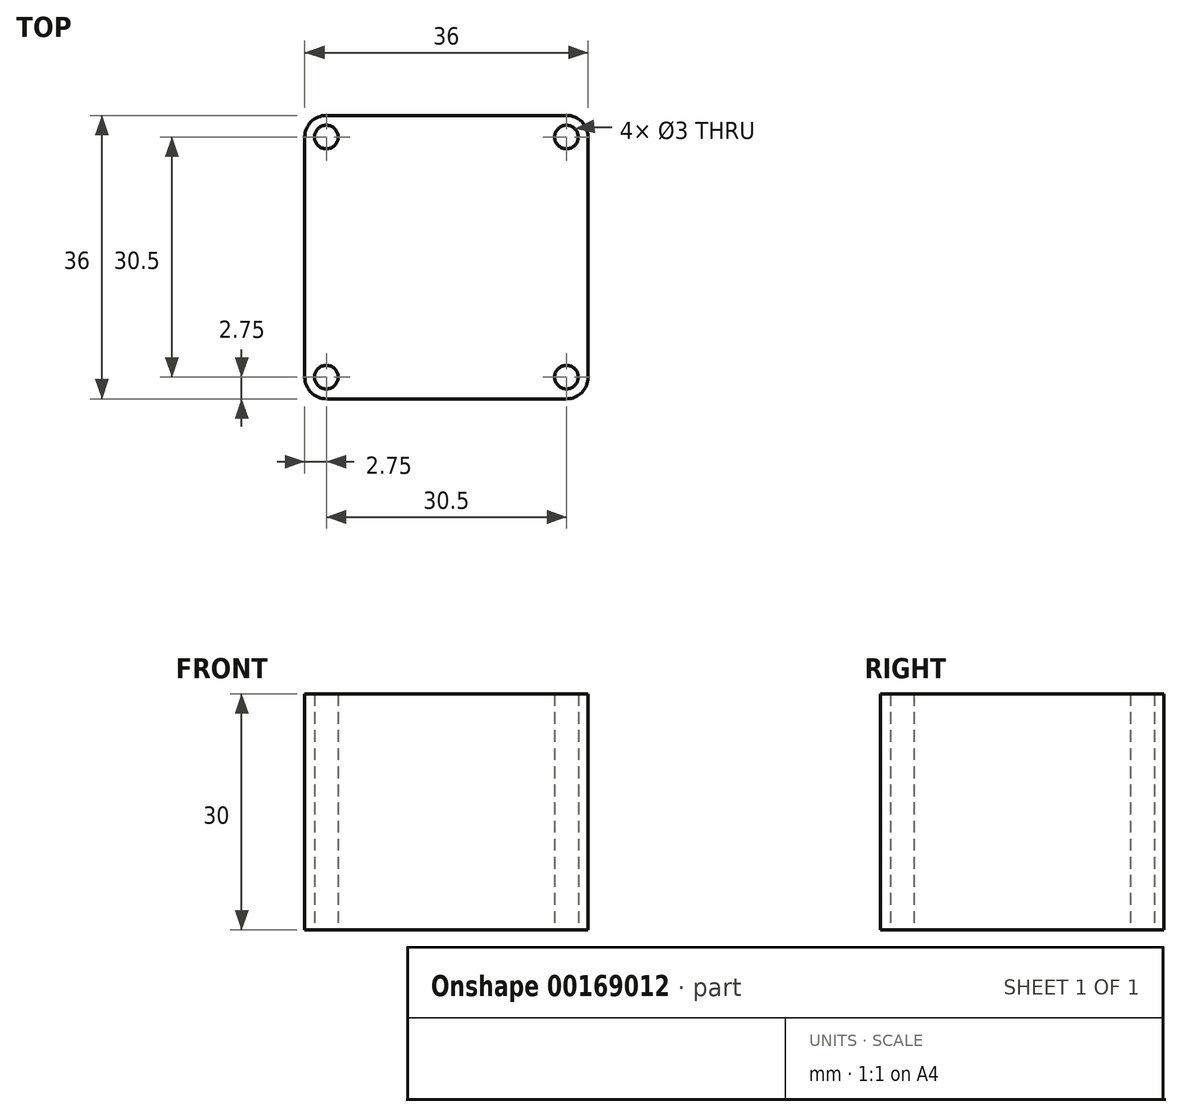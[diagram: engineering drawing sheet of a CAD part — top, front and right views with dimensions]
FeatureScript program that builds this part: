
annotation { "Feature Type Name" : "Feature", "Feature Type Description" : "" }
export const myFeature = defineFeature(function(context is Context, id is Id, definition is map)
    precondition{}
    {
        {
            var Q0;
            Q0=qCreatedBy(makeId("Top.planeOp"),FACE);
            var sketch = newSketch(context, id + "F0", { "sketchPlane" : qUnion([Q0])});
            skLineSegment(sketch, "E0.bottom", {"start": v(2.75, 36) * mm, "end": v(33.25, 36) * mm});
            skLineSegment(sketch, "E0.top", {"start": v(2.75, 0) * mm, "end": v(33.25, 0) * mm});
            skLineSegment(sketch, "E0.left", {"start": v(0, 33.25) * mm, "end": v(0, 2.75) * mm});
            skLineSegment(sketch, "E0.right", {"start": v(36, 33.25) * mm, "end": v(36, 2.75) * mm});
            skCircle(sketch, "E1", {"center": v(2.75, 2.75) * mm, "radius": 1.5 * mm});
            skCircle(sketch, "E2.0.1.0", {"center": v(2.75, 33.25) * mm, "radius": 1.5 * mm});
            skCircle(sketch, "E2.1.0.0", {"center": v(33.25, 2.75) * mm, "radius": 1.5 * mm});
            skCircle(sketch, "E2.1.1.0", {"center": v(33.25, 33.25) * mm, "radius": 1.5 * mm});
            skLineSegment(sketch, "E2.direction1", {"start": v(2.75, 2.75) * mm, "end": v(33.25, 2.75) * mm, "construction": true});
            skLineSegment(sketch, "E2.direction2", {"start": v(2.75, 2.75) * mm, "end": v(2.75, 33.25) * mm, "construction": true});
            skPoint(sketch, "E3.visualSharp", {"position": v(0, 36) * mm});
            skArc(sketch, "E3.filletArc", {"start": v(2.75, 36) * mm, "mid": v(0.8, 35.2) * mm, "end": v(0, 33.25) * mm});
            skPoint(sketch, "E4.visualSharp", {"position": v(36, 36) * mm});
            skArc(sketch, "E4.filletArc", {"start": v(36, 33.25) * mm, "mid": v(35.2, 35.2) * mm, "end": v(33.25, 36) * mm});
            skPoint(sketch, "E5.visualSharp", {"position": v(36, 0) * mm});
            skArc(sketch, "E5.filletArc", {"start": v(33.25, 0) * mm, "mid": v(35.2, 0.8) * mm, "end": v(36, 2.75) * mm});
            skPoint(sketch, "E6.visualSharp", {"position": v(0, 0) * mm});
            skArc(sketch, "E6.filletArc", {"start": v(0, 2.75) * mm, "mid": v(0.8, 0.8) * mm, "end": v(2.75, 0) * mm});
            skSolve(sketch);
        }
        {
            var Q0;
            Q0 = qSketchRegion(id + "F0", true);
            extrude(context, id + "F1", {"entities" : qUnion([Q0]), "depth" : 30 * mm});
        }
    });
